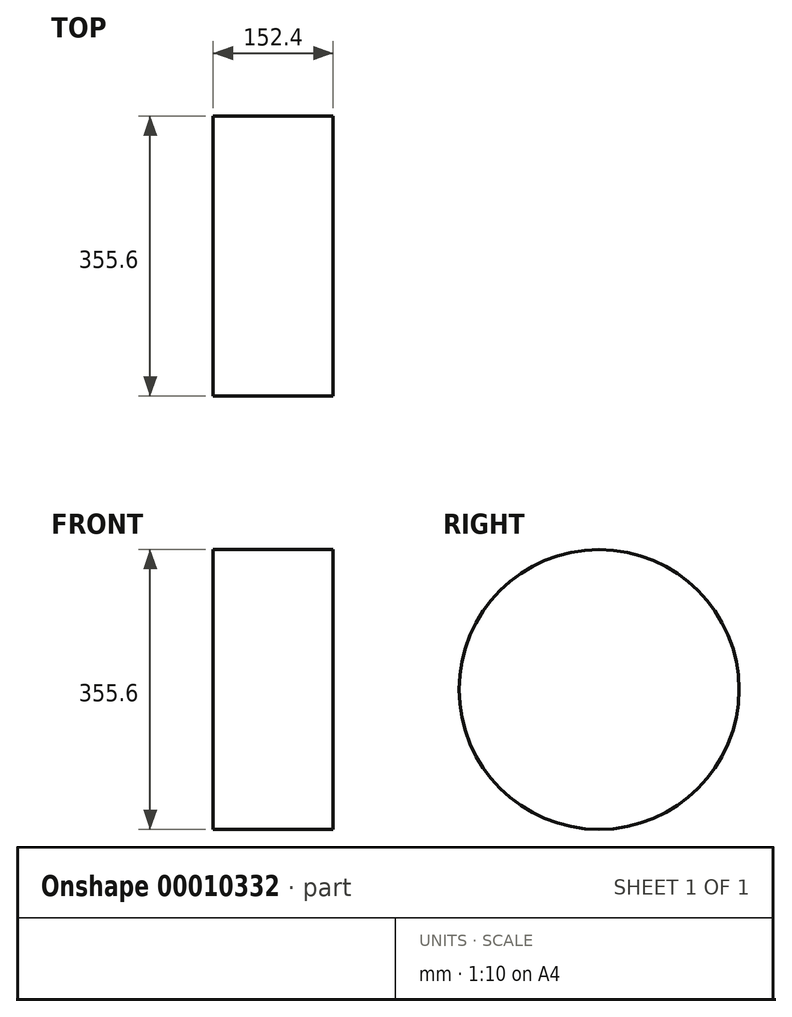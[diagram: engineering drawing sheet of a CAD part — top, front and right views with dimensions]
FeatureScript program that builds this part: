
annotation { "Feature Type Name" : "Feature", "Feature Type Description" : "" }
export const myFeature = defineFeature(function(context is Context, id is Id, definition is map)
    precondition{}
    {
        {
            var Q0;
            Q0=qCreatedBy(makeId("Right.planeOp"),FACE);
            var sketch = newSketch(context, id + "F0", { "sketchPlane" : qUnion([Q0])});
            skCircle(sketch, "E0", {"center": v(0, 0) * mm, "radius": 177.8 * mm});
            skSolve(sketch);
        }
        {
            var Q0;
            Q0 = qSketchRegion(id + "F0", true);
            extrude(context, id + "F1", {"entities" : qUnion([Q0]), "depth" : 152.4 * mm});
        }
    });
